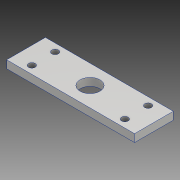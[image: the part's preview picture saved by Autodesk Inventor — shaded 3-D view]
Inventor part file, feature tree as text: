
AUTODESK INVENTOR PART (.ipt)
format: ipt  version: 2020 (Build 240168000, 168)  size: 99,328 bytes
history: native  units: mm
features: extrude x1, sketch x1
ambient origin geometry x8: Origin, YZ Plane, XZ Plane, XY Plane, X Axis, Y Axis, Z Axis, Center Point
bodies: Solid1 (feature_tree)
feature tree (2):
  extrude  "Extrusion1"  Depth=10.0mm
  sketch  "Sketch1"  dims[d0=165.0mm d1=82.5mm d2=25.6mm d3=50.0mm d4=25.0mm d5=8.5mm d6=22.5mm d7=22.5mm d8=22.5mm d9=22.5mm d10=10.0mm d11=10.0mm d12=10.0mm d13=10.0mm d14=10.0mm d15=0.0mm]
